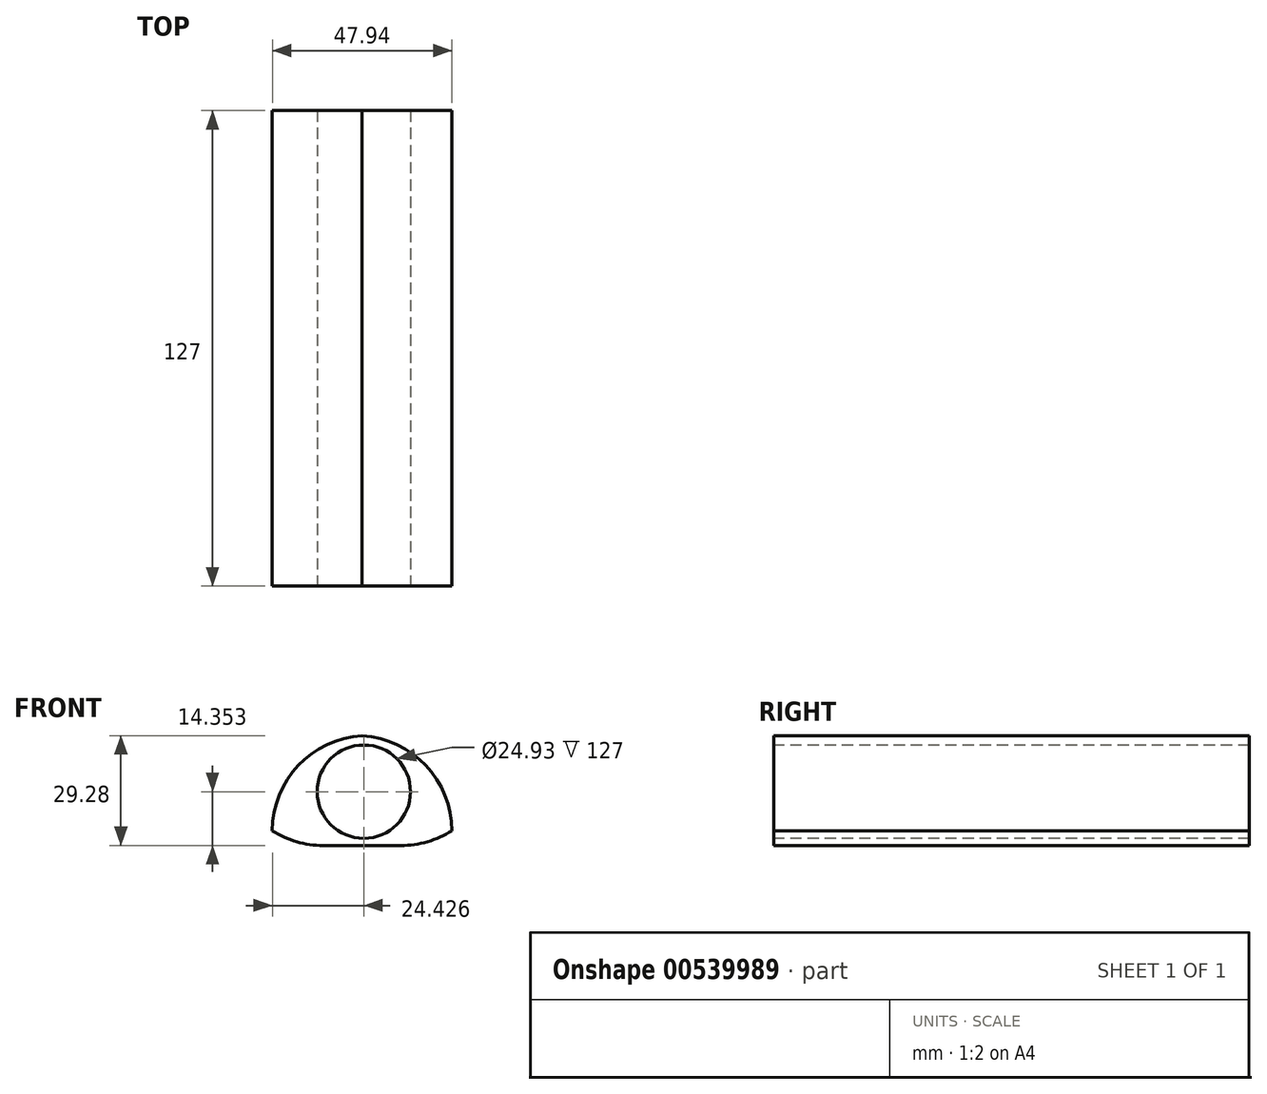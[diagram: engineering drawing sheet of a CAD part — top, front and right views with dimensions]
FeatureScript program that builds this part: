
annotation { "Feature Type Name" : "Feature", "Feature Type Description" : "" }
export const myFeature = defineFeature(function(context is Context, id is Id, definition is map)
    precondition{}
    {
        {
            var Q0;
            Q0=qCreatedBy(makeId("Front.planeOp"),FACE);
            var sketch = newSketch(context, id + "F0", { "sketchPlane" : qUnion([Q0])});
            skLineSegment(sketch, "E0.bottom", {"start": v(0, 0) * mm, "end": v(-47.94, 0) * mm});
            skLineSegment(sketch, "E0.top", {"start": v(0, 29.32) * mm, "end": v(-47.94, 29.32) * mm});
            skLineSegment(sketch, "E0.left", {"start": v(0, 0) * mm, "end": v(0, 29.32) * mm});
            skLineSegment(sketch, "E0.right", {"start": v(-47.94, 0) * mm, "end": v(-47.94, 29.32) * mm});
            skSolve(sketch);
        }
        {
            var Q0;
            Q0 = qSketchRegion(id + "F0", true);
            extrude(context, id + "F1", {"entities" : qUnion([Q0]), "depth" : 127 * mm, "offsetDistance" : 25.4 * mm});
        }
        {
            var Q0;
            Q0=makeQuery(id+"F1.opExtrude","CAP_FACE",FACE,{"disambiguationData":[OSD([sQuery(id+"F0.wireOp",EDGE,"E0.bottom"),sQuery(id+"F0.wireOp",EDGE,"E0.top"),sQuery(id+"F0.wireOp",EDGE,"E0.left"),sQuery(id+"F0.wireOp",EDGE,"E0.right")])],"isStart":false});
            var sketch = newSketch(context, id + "F2", { "sketchPlane" : qUnion([Q0])});
            skSolve(sketch);
        }
        {
            var Q0;
            Q0=makeQuery(id+"F2.imprint","IMPRINT",FACE,{"disambiguationData":[TD([[makeQuery(id+"F2.imprint","IMPRINT",EDGE,{"derivedFrom":makeQuery(id+"F1.opExtrude","CAP_EDGE",EDGE,{"disambiguationData":[OSD([sQuery(id+"F0.wireOp",EDGE,"E0.bottom")])],"isStart":false})}),-1.0]])]});
            var sketch = newSketch(context, id + "F3", { "sketchPlane" : qUnion([Q0])});
            skCircle(sketch, "E1", {"center": v(-23.51, 14.35) * mm, "radius": 12.46 * mm});
            skSolve(sketch);
        }
        {
            var Q0;
            Q0 = qSketchRegion(id + "F3", true);
            extrude(context, id + "F4", {"entities" : qUnion([Q0]), "operationType" : NewBodyOperationType.REMOVE, "oppositeDirection" : true, "depth" : 127 * mm, "offsetDistance" : 25.4 * mm});
        }
        {
            var Q0;
            Q0=makeQuery(id+"F1.opExtrude","SWEPT_EDGE",EDGE,{"disambiguationData":[OSD([sQuery(id+"F0.wireOp",EDGE,"E0.top"),sQuery(id+"F0.wireOp",EDGE,"E0.right")])]});
            var Q1;
            Q1=makeQuery(id+"F1.opExtrude","SWEPT_EDGE",EDGE,{"disambiguationData":[OSD([sQuery(id+"F0.wireOp",EDGE,"E0.top"),sQuery(id+"F0.wireOp",EDGE,"E0.left")])]});
            fillet(context, id + "F5", {"entities" : qUnion([Q0, Q1]), "radius" : 25.4 * mm, "tangentPropagation" : true, "allowEdgeOverflow" : false});
        }
        {
            var Q0;
            Q0=makeQuery(id+"F1.opExtrude","SWEPT_EDGE",EDGE,{"disambiguationData":[OSD([sQuery(id+"F0.wireOp",EDGE,"E0.bottom"),sQuery(id+"F0.wireOp",EDGE,"E0.left")])]});
            fillet(context, id + "F6", {"entities" : qUnion([Q0]), "radius" : 25.4 * mm, "tangentPropagation" : true, "allowEdgeOverflow" : false});
        }
        {
            var Q0;
            Q0=makeQuery(id+"F1.opExtrude","SWEPT_EDGE",EDGE,{"disambiguationData":[OSD([sQuery(id+"F0.wireOp",EDGE,"E0.bottom"),sQuery(id+"F0.wireOp",EDGE,"E0.right")])]});
            fillet(context, id + "F7", {"entities" : qUnion([Q0]), "radius" : 25.4 * mm, "tangentPropagation" : true, "allowEdgeOverflow" : false});
        }
    });
